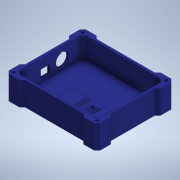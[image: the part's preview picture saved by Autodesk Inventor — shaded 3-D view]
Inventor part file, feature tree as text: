
AUTODESK INVENTOR PART (.ipt)
format: ipt  version: 2020 (Build 240168000, 168)  size: 390,144 bytes
history: native  units: mm
features: projected_geometry x13, sketch x8, extrude x5, hole x2, chamfer x1
ambient origin geometry x8: Origin, YZ Plane, XZ Plane, XY Plane, X Axis, Y Axis, Z Axis, Center Point
bodies: Body1 (feature_tree)
feature tree (29):
  extrude  "Extrusion2"  Depth=100.0mm
  extrude  "Extrusion3"  Depth=15.0mm
  extrude  "Extrusion4"  Depth=4.0mm
  chamfer  "Chamfer1"  Distance=3.0mm
  hole  "Hole1"  [1 undecoded]
  extrude  "Extrusion5"  Depth=30.0mm
  hole  "Hole2"  [1 undecoded]
  extrude  "Extrusion6"  Depth=3.0mm
  sketch  "Sketch9"  dims[d21=101.6mm d23=3.0mm d24=3.0mm d25=14.0mm d26=1.3mm d27=50.8mm d29=2.5mm d30=5.1mm d31=27.9mm d32=15.2mm d33=24.1mm d34=96.52mm d35=30.0mm d36=50.0mm d37=10.0mm d38=10.0mm d39=75.0mm d40=85.0mm d41=5.0mm d42=3.0mm d43=0.0mm d44=3.0mm d45=2.0mm d46=45.0deg d47=4.0mm d48=6.0mm d49=4.0mm d50=2.0mm d51=90.0deg d52=5.0mm d53=0.0mm d55=11.5mm d56=12.5mm d57=1.7mm d58=9.25mm d59=10.0mm d60=0.0mm d61=4.0mm d62=6.0mm d63=4.0mm d64=2.0mm d65=90.0deg d66=5.0mm d67=0.0mm d68=18.0mm d69=20.0mm d70=3.0mm d71=13.0mm d72=13.0mm d73=10.0mm d74=0.0mm]
  sketch  "Sketch1"  dims[d4=120.0mm d5=100.0mm]
  sketch  "Sketch2"  dims[d6=45.0deg d7=15.0mm]
  projected_geometry  "Projected Loop1"
  sketch  "Sketch4"  dims[d8=4.0mm d9=4.0mm]
  projected_geometry  "Projected Loop2"
  projected_geometry  "Projected Loop3"
  sketch  "Sketch5"  dims[d12=45.0deg]
  projected_geometry  "Projected Loop4"
  projected_geometry  "Projected Loop5"
  sketch  "Sketch6"  dims[d13=4.0mm d14=3.0mm d15=0.0mm]
  projected_geometry  "Projected Loop6"
  projected_geometry  "Projected Loop7"
  projected_geometry  "Projected Loop8"
  projected_geometry  "Projected Loop9"
  projected_geometry  "Projected Loop10"
  sketch  "Sketch7"  dims[d16=3.0mm d17=10.0mm]
  projected_geometry  "Projected Loop11"
  sketch  "Sketch8"  dims[d18=30.0mm d19=0.0mm d20=53.34mm]
  projected_geometry  "Projected Loop12"
  projected_geometry  "Projected Loop13"
note: 2 required parameter values undecoded (feature->parameter linkage not recoverable at this tier; creation-order binding heuristic only, values carry confidence <= 0.55)
